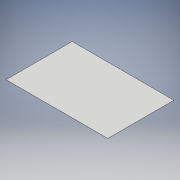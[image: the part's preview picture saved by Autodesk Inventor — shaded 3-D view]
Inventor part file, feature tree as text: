
AUTODESK INVENTOR PART (.ipt)
format: ipt  version: 2017 (Build 210142000, 142)  size: 95,232 bytes
history: native  units: mm
features: sheet_metal_op x1, sketch x1, other x1
ambient origin geometry x8: Origin, YZ Plane, XZ Plane, XY Plane, X Axis, Y Axis, Z Axis, Center Point
bodies: Solid1 (feature_tree)
feature tree (3):
  sheet_metal_op  "Face1"
  sketch  "Sketch1"  dims[d0=400.0mm d1=260.0mm d2=0.5mm]
  other  "Plate1"
